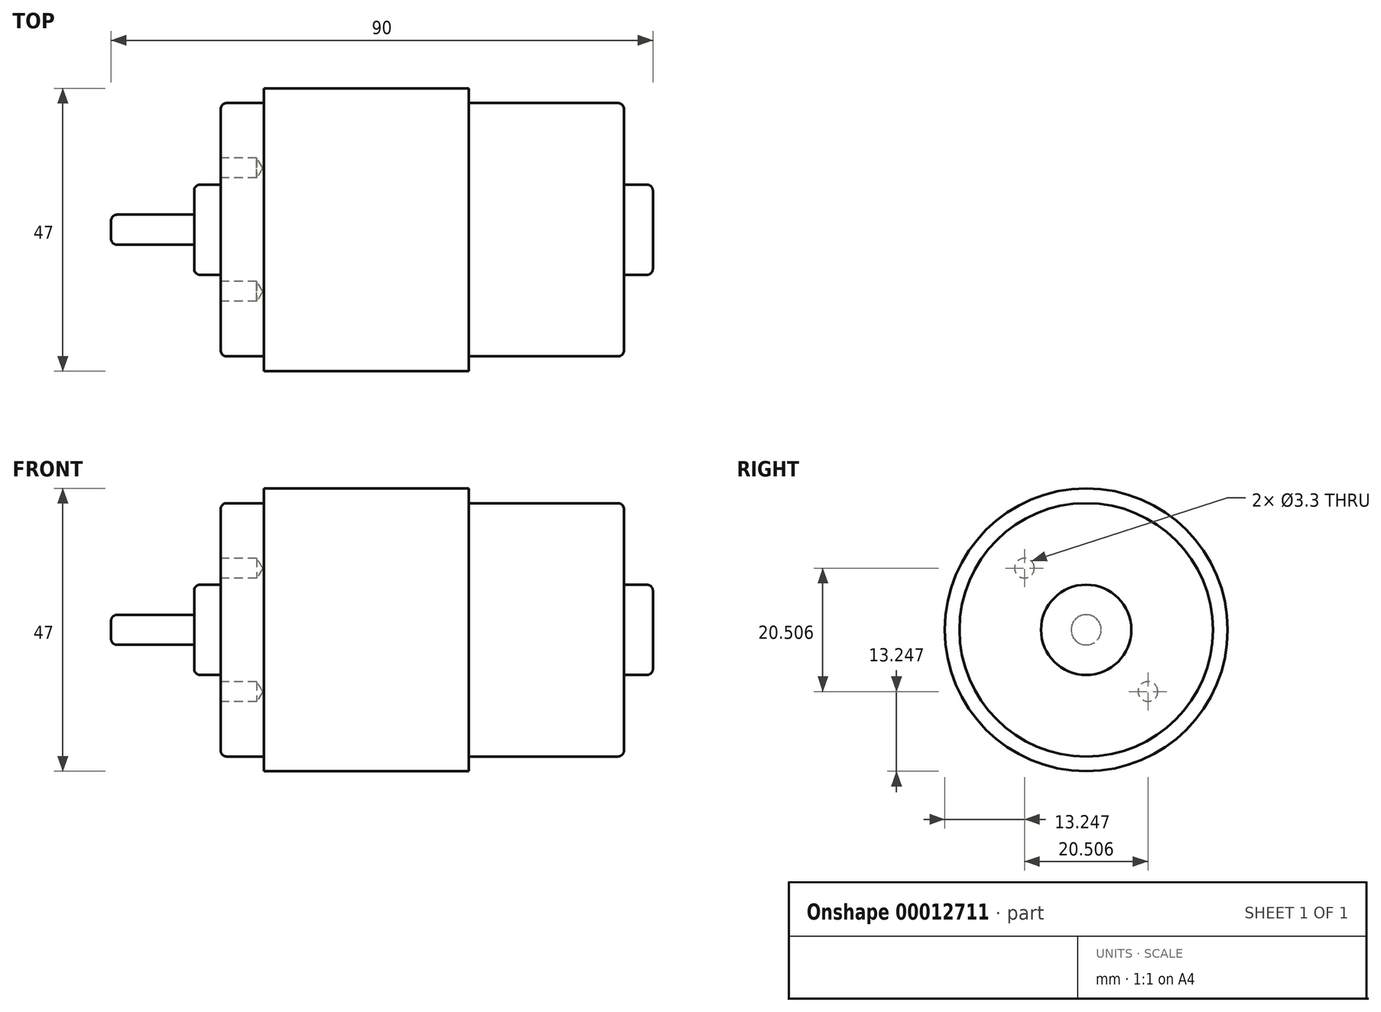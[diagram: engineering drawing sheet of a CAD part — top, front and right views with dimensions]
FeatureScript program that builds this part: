
annotation { "Feature Type Name" : "Feature", "Feature Type Description" : "" }
export const myFeature = defineFeature(function(context is Context, id is Id, definition is map)
    precondition{}
    {
        {
            var Q0;
            Q0=qCreatedBy(makeId("Top.planeOp"),FACE);
            var sketch = newSketch(context, id + "F0", { "sketchPlane" : qUnion([Q0])});
            skLineSegment(sketch, "E0", {"start": v(0, 7.5) * mm, "end": v(-4.4, 7.5) * mm});
            skLineSegment(sketch, "E1", {"start": v(-4.4, 7.5) * mm, "end": v(-4.4, 2.5) * mm});
            skLineSegment(sketch, "E2", {"start": v(-4.4, 2.5) * mm, "end": v(-18.2, 2.5) * mm});
            skLineSegment(sketch, "E3", {"start": v(-18.2, 2.5) * mm, "end": v(-18.2, 0) * mm});
            skLineSegment(sketch, "E4", {"start": v(0, 7.5) * mm, "end": v(0, 21.05) * mm});
            skLineSegment(sketch, "E5", {"start": v(0, 21.05) * mm, "end": v(7.2, 21.05) * mm});
            skLineSegment(sketch, "E6", {"start": v(7.2, 21.05) * mm, "end": v(7.2, 23.5) * mm});
            skLineSegment(sketch, "E7", {"start": v(7.2, 23.5) * mm, "end": v(41.2, 23.5) * mm});
            skLineSegment(sketch, "E8", {"start": v(41.2, 23.5) * mm, "end": v(41.2, 21.05) * mm});
            skLineSegment(sketch, "E9", {"start": v(41.2, 21.05) * mm, "end": v(67, 21.05) * mm});
            skLineSegment(sketch, "E10", {"start": v(67, 21.05) * mm, "end": v(67, 7.5) * mm});
            skLineSegment(sketch, "E11", {"start": v(67, 7.5) * mm, "end": v(71.8, 7.5) * mm});
            skLineSegment(sketch, "E12", {"start": v(71.8, 7.5) * mm, "end": v(71.8, 0) * mm});
            skLineSegment(sketch, "E13", {"start": v(-18.2, 0) * mm, "end": v(71.8, 0) * mm, "construction": true});
            skLineSegment(sketch, "E14", {"start": v(-18.2, 0) * mm, "end": v(71.8, 0) * mm});
            skSolve(sketch);
        }
        {
            var Q0;
            Q0=makeQuery(id+"F0.imprint","IMPRINT",FACE,{"disambiguationData":[TD([[makeQuery(id+"F0.imprint","IMPRINT",EDGE,{"derivedFrom":sQuery(id+"F0.wireOp",EDGE,"E0")}),1.0]])]});
            var Q1;
            Q1=sQuery(id+"F0.wireOp",EDGE,"E14");
            revolve(context, id + "F1", {"entities" : qUnion([Q0]), "axis" : qUnion([Q1]), "revolveType" : RevolveType.FULL});
        }
        {
            var Q0;
            Q0=makeQuery(id+"F1.opRevolve","SWEPT_EDGE",EDGE,{"disambiguationData":[OSD([sQuery(id+"F0.wireOp",EDGE,"E9"),sQuery(id+"F0.wireOp",EDGE,"E10")])]});
            var Q1;
            Q1=makeQuery(id+"F1.opRevolve","SWEPT_EDGE",EDGE,{"disambiguationData":[OSD([sQuery(id+"F0.wireOp",EDGE,"E11"),sQuery(id+"F0.wireOp",EDGE,"E12")])]});
            var Q2;
            Q2=makeQuery(id+"F1.opRevolve","SWEPT_EDGE",EDGE,{"disambiguationData":[OSD([sQuery(id+"F0.wireOp",EDGE,"E4"),sQuery(id+"F0.wireOp",EDGE,"E5")])]});
            var Q3;
            Q3=makeQuery(id+"F1.opRevolve","SWEPT_EDGE",EDGE,{"disambiguationData":[OSD([sQuery(id+"F0.wireOp",EDGE,"E0"),sQuery(id+"F0.wireOp",EDGE,"E1")])]});
            var Q4;
            Q4=makeQuery(id+"F1.opRevolve","SWEPT_EDGE",EDGE,{"disambiguationData":[OSD([sQuery(id+"F0.wireOp",EDGE,"E2"),sQuery(id+"F0.wireOp",EDGE,"E3")])]});
            fillet(context, id + "F2", {"entities" : qUnion([Q0, Q1, Q2, Q3, Q4]), "radius" : 1 * mm, "tangentPropagation" : true, "allowEdgeOverflow" : false});
        }
        {
            var Q0;
            Q0=makeQuery(id+"F1.opRevolve","SWEPT_FACE",FACE,{"disambiguationData":[OSD([sQuery(id+"F0.wireOp",EDGE,"E4")])]});
            var sketch = newSketch(context, id + "F3", { "sketchPlane" : qUnion([Q0])});
            skLineSegment(sketch, "E15.rect.bottom", {"start": v(-25, 25) * mm, "end": v(25, 25) * mm, "construction": true});
            skLineSegment(sketch, "E15.rect.top", {"start": v(-25, -25) * mm, "end": v(25, -25) * mm, "construction": true});
            skLineSegment(sketch, "E15.rect.left", {"start": v(-25, 25) * mm, "end": v(-25, -25) * mm, "construction": true});
            skLineSegment(sketch, "E15.rect.right", {"start": v(25, 25) * mm, "end": v(25, -25) * mm, "construction": true});
            skPoint(sketch, "E15.rect.middle", {"position": v(0, 0) * mm});
            skLineSegment(sketch, "E16", {"start": v(-25, 25) * mm, "end": v(25, -25) * mm, "construction": true});
            skLineSegment(sketch, "E17", {"start": v(25, 25) * mm, "end": v(-25, -25) * mm, "construction": true});
            skCircle(sketch, "E18", {"center": v(0, 0) * mm, "radius": 14.5 * mm, "construction": true});
            skPoint(sketch, "E19", {"position": v(10.25, 10.25) * mm});
            skPoint(sketch, "E20", {"position": v(-10.25, -10.25) * mm});
            skSolve(sketch);
        }
        {
            var Q0;
            Q0=sQuery(id+"F3.wireOp",VERTEX,"E19");
            var Q1;
            Q1=sQuery(id+"F3.wireOp",VERTEX,"E20");
            var Q2;
            Q2=makeQuery(id+"F1.opRevolve","SWEPT_BODY",BODY,{"disambiguationData":[OSD([sQuery(id+"F0.wireOp",EDGE,"E0"),sQuery(id+"F0.wireOp",EDGE,"E1"),sQuery(id+"F0.wireOp",EDGE,"E2"),sQuery(id+"F0.wireOp",EDGE,"E3"),sQuery(id+"F0.wireOp",EDGE,"E4"),sQuery(id+"F0.wireOp",EDGE,"E5"),sQuery(id+"F0.wireOp",EDGE,"E6"),sQuery(id+"F0.wireOp",EDGE,"E7"),sQuery(id+"F0.wireOp",EDGE,"E8"),sQuery(id+"F0.wireOp",EDGE,"E9"),sQuery(id+"F0.wireOp",EDGE,"E10"),sQuery(id+"F0.wireOp",EDGE,"E11"),sQuery(id+"F0.wireOp",EDGE,"E12"),sQuery(id+"F0.wireOp",EDGE,"E14")])]});
            hole(context, id + "F4", {"style" : HoleStyle.SIMPLE, "holeDiameter" : 3.3 * mm, "endStyle" : HoleEndStyle.BLIND, "holeDepth" : 6 * mm, "locations" : qUnion([Q0, Q1]), "scope" : qUnion([Q2])});
        }
    });
